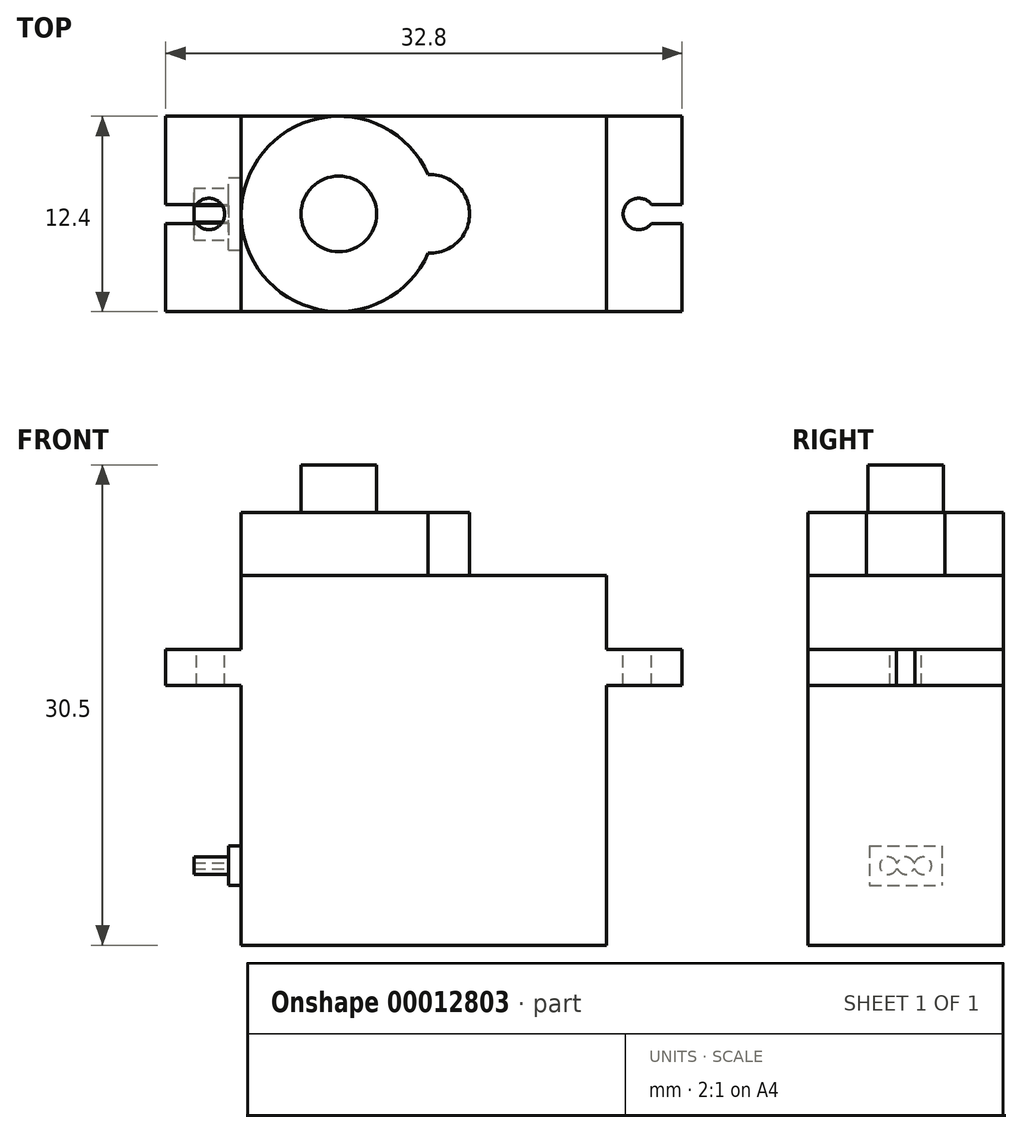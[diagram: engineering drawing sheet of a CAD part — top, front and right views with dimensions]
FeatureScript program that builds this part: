
annotation { "Feature Type Name" : "Feature", "Feature Type Description" : "" }
export const myFeature = defineFeature(function(context is Context, id is Id, definition is map)
    precondition{}
    {
        {
            var Q0;
            Q0=qCreatedBy(makeId("Top.planeOp"),FACE);
            var sketch = newSketch(context, id + "F0", { "sketchPlane" : qUnion([Q0])});
            skArc(sketch, "E0", {"start": v(0.27, 2.5) * mm, "mid": v(-11.6, 0) * mm, "end": v(0.27, -2.5) * mm});
            skLineSegment(sketch, "E1.bottom", {"start": v(-16.4, 6.2) * mm, "end": v(16.4, 6.2) * mm});
            skLineSegment(sketch, "E1.top", {"start": v(-16.4, -6.2) * mm, "end": v(16.4, -6.2) * mm});
            skLineSegment(sketch, "E2", {"start": v(-11.6, 6.2) * mm, "end": v(-11.6, -6.2) * mm});
            skLineSegment(sketch, "E3", {"start": v(11.6, 6.2) * mm, "end": v(11.6, -6.2) * mm});
            skArc(sketch, "E4", {"start": v(-14.45, -0.6) * mm, "mid": v(-12.65, 0) * mm, "end": v(-14.45, 0.6) * mm});
            skLineSegment(sketch, "E5", {"start": v(0, 6.2) * mm, "end": v(0, -6.2) * mm, "construction": true});
            skArc(sketch, "E6", {"start": v(0.27, -2.5) * mm, "mid": v(2.9, 0) * mm, "end": v(0.27, 2.5) * mm});
            skCircle(sketch, "E7", {"center": v(-5.4, 0) * mm, "radius": 2.4 * mm});
            skLineSegment(sketch, "E8", {"start": v(-16.4, 6.2) * mm, "end": v(-16.4, -6.2) * mm});
            skLineSegment(sketch, "E9", {"start": v(16.4, 6.2) * mm, "end": v(16.4, -6.2) * mm});
            skLineSegment(sketch, "E10", {"start": v(-14.45, 0.6) * mm, "end": v(-16.4, 0.6) * mm});
            skLineSegment(sketch, "E11", {"start": v(-14.45, -0.6) * mm, "end": v(-16.4, -0.6) * mm});
            skArc(sketch, "E12.0.MirrorCS", {"start": v(14.45, -0.6) * mm, "mid": v(12.65, 0) * mm, "end": v(14.45, 0.6) * mm});
            skLineSegment(sketch, "E13.0.MirrorCS", {"start": v(14.45, 0.6) * mm, "end": v(16.4, 0.6) * mm});
            skLineSegment(sketch, "E14.0.MirrorCS", {"start": v(14.45, -0.6) * mm, "end": v(16.4, -0.6) * mm});
            skSolve(sketch);
        }
        {
            var Q0;
            {var subQ1=sQuery(id+"F0.wireOp",EDGE,"E3");Q0=makeQuery(id+"F0.imprint","IMPRINT",FACE,{"disambiguationData":[TD([[makeQuery(id+"F0.imprint","IMPRINT",EDGE,{"derivedFrom":subQ1}),-1.0]])]});}
            var Q1;
            {var subQ0=sQuery(id+"F0.wireOp",EDGE,"E6");Q1=makeQuery(id+"F0.imprint","IMPRINT",FACE,{"disambiguationData":[TD([[makeQuery(id+"F0.imprint","IMPRINT",EDGE,{"derivedFrom":subQ0}),1.0]])]});}
            var Q2;
            Q2=makeQuery(id+"F0.imprint","IMPRINT",FACE,{"disambiguationData":[TD([[makeQuery(id+"F0.imprint","IMPRINT",EDGE,{"derivedFrom":sQuery(id+"F0.wireOp",EDGE,"E7")}),1.0]])]});
            var Q3;
            {var subQ1=sQuery(id+"F0.wireOp",EDGE,"E0");var subQ3=sQuery(id+"F0.wireOp",EDGE,"E1.top");var subQ5=makeQuery(id+"F0.imprint","INTERSECT",VERTEX,{"derivedFrom":[subQ1,subQ3]});Q3=makeQuery(id+"F0.imprint","IMPRINT",FACE,{"disambiguationData":[TD([[makeQuery(id+"F0.imprint","IMPRINT",EDGE,{"disambiguationData":[TD([[subQ5,1.0]])],"derivedFrom":subQ1}),-1.0]])]});}
            var Q4;
            {var subQ1=sQuery(id+"F0.wireOp",EDGE,"E0");var subQ3=sQuery(id+"F0.wireOp",EDGE,"E1.bottom");var subQ5=makeQuery(id+"F0.imprint","INTERSECT",VERTEX,{"derivedFrom":[subQ1,subQ3]});Q4=makeQuery(id+"F0.imprint","IMPRINT",FACE,{"disambiguationData":[TD([[makeQuery(id+"F0.imprint","IMPRINT",EDGE,{"disambiguationData":[TD([[subQ5,-1.0]])],"derivedFrom":subQ1}),-1.0]])]});}
            extrude(context, id + "F1", {"entities" : qUnion([Q0, Q1, Q2, Q3, Q4]), "oppositeDirection" : true, "depth" : 23.5 * mm});
        }
        {
            var Q0;
            {var subQ0=sQuery(id+"F0.wireOp",EDGE,"E6");Q0=makeQuery(id+"F0.imprint","IMPRINT",FACE,{"disambiguationData":[TD([[makeQuery(id+"F0.imprint","IMPRINT",EDGE,{"derivedFrom":subQ0}),1.0]])]});}
            extrude(context, id + "F2", {"entities" : qUnion([Q0]), "operationType" : NewBodyOperationType.ADD, "depth" : 4 * mm});
        }
        {
            var Q0;
            Q0=makeQuery(id+"F0.imprint","IMPRINT",FACE,{"disambiguationData":[TD([[makeQuery(id+"F0.imprint","IMPRINT",EDGE,{"derivedFrom":sQuery(id+"F0.wireOp",EDGE,"E7")}),1.0]])]});
            extrude(context, id + "F3", {"entities" : qUnion([Q0]), "operationType" : NewBodyOperationType.ADD, "depth" : 7 * mm});
        }
        {
            var Q0;
            {var subQ7=sQuery(id+"F0.wireOp",EDGE,"E3");Q0=makeQuery(id+"F0.imprint","IMPRINT",FACE,{"disambiguationData":[TD([[makeQuery(id+"F0.imprint","IMPRINT",EDGE,{"derivedFrom":subQ7}),1.0]])]});}
            var Q1;
            Q1=makeQuery(id+"F0.imprint","IMPRINT",FACE,{"disambiguationData":[TD([[makeQuery(id+"F0.imprint","IMPRINT",EDGE,{"derivedFrom":sQuery(id+"F0.wireOp",EDGE,"E4")}),-1.0]])]});
            extrude(context, id + "F4", {"entities" : qUnion([Q0, Q1]), "operationType" : NewBodyOperationType.ADD, "oppositeDirection" : true, "depth" : (2.3 + 23.5 - 18.8) * mm, "hasSecondDirection" : true, "secondDirectionOppositeDirection" : true, "secondDirectionDepth" : (23.5 - 18.8) * mm});
        }
        {
            var Q0;
            {var subQ0=sQuery(id+"F0.wireOp",EDGE,"E2");var subQ1=sQuery(id+"F0.wireOp",EDGE,"E1.top");var subQ2=sQuery(id+"F0.wireOp",EDGE,"E3");var subQ5=sQuery(id+"F0.wireOp",EDGE,"E1.bottom");Q0=makeQuery(id+"F4.boolean.opBoolean","SPLIT",FACE,{"disambiguationData":[TD([makeQuery(id+"F1.opExtrude","CAP_FACE",FACE,{"disambiguationData":[OSD([subQ5,subQ1,subQ0,subQ2])],"isStart":false})])],"derivedFrom":makeQuery(id+"F1.opExtrude","SWEPT_FACE",FACE,{"disambiguationData":[OSD([subQ0])]})});}
            var sketch = newSketch(context, id + "F5", { "sketchPlane" : qUnion([Q0])});
            skLineSegment(sketch, "E15", {"start": v(0, -23.5) * mm, "end": v(0, -17.2) * mm, "construction": true});
            skLineSegment(sketch, "E16.rect.bottom", {"start": v(2.3, -17.2) * mm, "end": v(-2.3, -17.2) * mm});
            skLineSegment(sketch, "E16.rect.top", {"start": v(2.3, -19.7) * mm, "end": v(-2.3, -19.7) * mm});
            skLineSegment(sketch, "E16.rect.left", {"start": v(2.3, -17.2) * mm, "end": v(2.3, -19.7) * mm});
            skLineSegment(sketch, "E16.rect.right", {"start": v(-2.3, -17.2) * mm, "end": v(-2.3, -19.7) * mm});
            skPoint(sketch, "E16.rect.middle", {"position": v(0, -18.45) * mm});
            skCircle(sketch, "E17", {"center": v(0, -18.45) * mm, "radius": 0.55 * mm});
            skCircle(sketch, "E18", {"center": v(1.1, -18.45) * mm, "radius": 0.55 * mm});
            skCircle(sketch, "E19", {"center": v(-1.1, -18.45) * mm, "radius": 0.55 * mm});
            skLineSegment(sketch, "E20.rect.bottom", {"start": v(1.1, -18.26) * mm, "end": v(-1.1, -18.26) * mm});
            skLineSegment(sketch, "E20.rect.top", {"start": v(1.1, -18.64) * mm, "end": v(-1.1, -18.64) * mm});
            skLineSegment(sketch, "E20.rect.left", {"start": v(1.1, -18.26) * mm, "end": v(1.1, -18.64) * mm});
            skLineSegment(sketch, "E20.rect.right", {"start": v(-1.1, -18.26) * mm, "end": v(-1.1, -18.64) * mm});
            skSolve(sketch);
        }
        {
            var Q0;
            Q0=makeQuery(id+"F5.imprint","IMPRINT",FACE,{"disambiguationData":[TD([[makeQuery(id+"F5.imprint","IMPRINT",EDGE,{"derivedFrom":sQuery(id+"F5.wireOp",EDGE,"E16.rect.bottom")}),1.0]])]});
            extrude(context, id + "F6", {"entities" : qUnion([Q0]), "operationType" : NewBodyOperationType.ADD, "depth" : .8 * mm});
        }
        {
            var Q0;
            {var subQ0=sQuery(id+"F0.wireOp",EDGE,"E2");var subQ1=sQuery(id+"F0.wireOp",EDGE,"E1.top");var subQ2=sQuery(id+"F0.wireOp",EDGE,"E3");var subQ5=sQuery(id+"F0.wireOp",EDGE,"E1.bottom");var subQ10=sQuery(id+"F5.wireOp",EDGE,"E18");Q0=makeQuery(id+"F6.boolean.opBoolean","SPLIT",FACE,{"disambiguationData":[TD([makeQuery(id+"F6.opExtrude","SWEPT_FACE",FACE,{"disambiguationData":[OSD([subQ10])]})])],"derivedFrom":makeQuery(id+"F4.boolean.opBoolean","SPLIT",FACE,{"disambiguationData":[TD([makeQuery(id+"F1.opExtrude","CAP_FACE",FACE,{"disambiguationData":[OSD([subQ5,subQ1,subQ0,subQ2])],"isStart":false})])],"derivedFrom":makeQuery(id+"F1.opExtrude","SWEPT_FACE",FACE,{"disambiguationData":[OSD([subQ0])]})})});}
            extrude(context, id + "F7", {"entities" : qUnion([Q0]), "operationType" : NewBodyOperationType.ADD, "depth" : 3 * mm});
        }
    });
